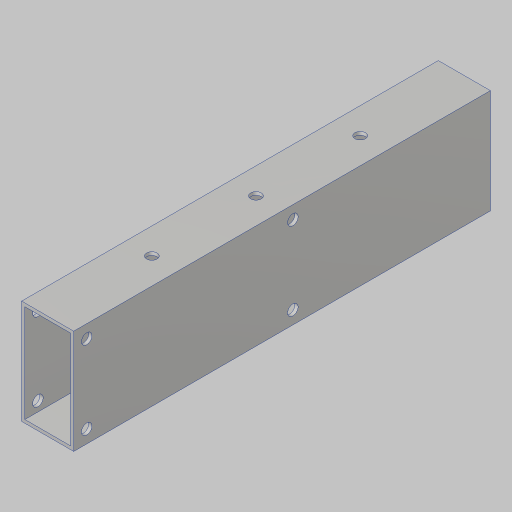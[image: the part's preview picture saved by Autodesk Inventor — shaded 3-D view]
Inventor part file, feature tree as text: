
AUTODESK INVENTOR PART (.ipt)
format: ipt  version: 2023.5 (Build 275446000, 446)  size: 144,896 bytes
history: native  units: in
note: dims shown in document units (in); Inventor stores cm internally (conversion verified against a paired STEP export)
features: hole x3, sketch x3, extrude x1, projected_geometry x1
ambient origin geometry x8: Origin, YZ Plane, XZ Plane, XY Plane, X Axis, Y Axis, Z Axis, Center Point
bodies: Solid1 (feature_tree)
feature tree (8):
  extrude  "Extrusion1"  Depth=4.0in
  hole  "Hole1"  [1 undecoded]
  hole  "Hole3"  [1 undecoded]
  hole  "Hole2"  [1 undecoded]
  sketch  "Sketch2"  dims[d4=0.0in d5=4.0in]
  projected_geometry  "Projected Loop1"
  sketch  "Sketch3"  dims[d6=0.201in d7=0.75in d8=0.385in d9=0.25in d10=0.5635in d11=1.0in d12=0.8108in d14=4.7244in]
  sketch  "Sketch4"  dims[d15=3.7402in d16=4.2323in d17=1.5in d18=0.156in d19=0.38in d20=0.375in d21=0.25in d22=0.5635in d23=1.0in d24=0.8108in d25=4.2323in d27=0.25in d28=1.5in d29=0.201in d30=0.38in d31=0.385in d32=0.25in d33=0.5635in d34=1.0in d35=0.8108in]
note: 3 required parameter values undecoded (feature->parameter linkage not recoverable at this tier; creation-order binding heuristic only, values carry confidence <= 0.55)
